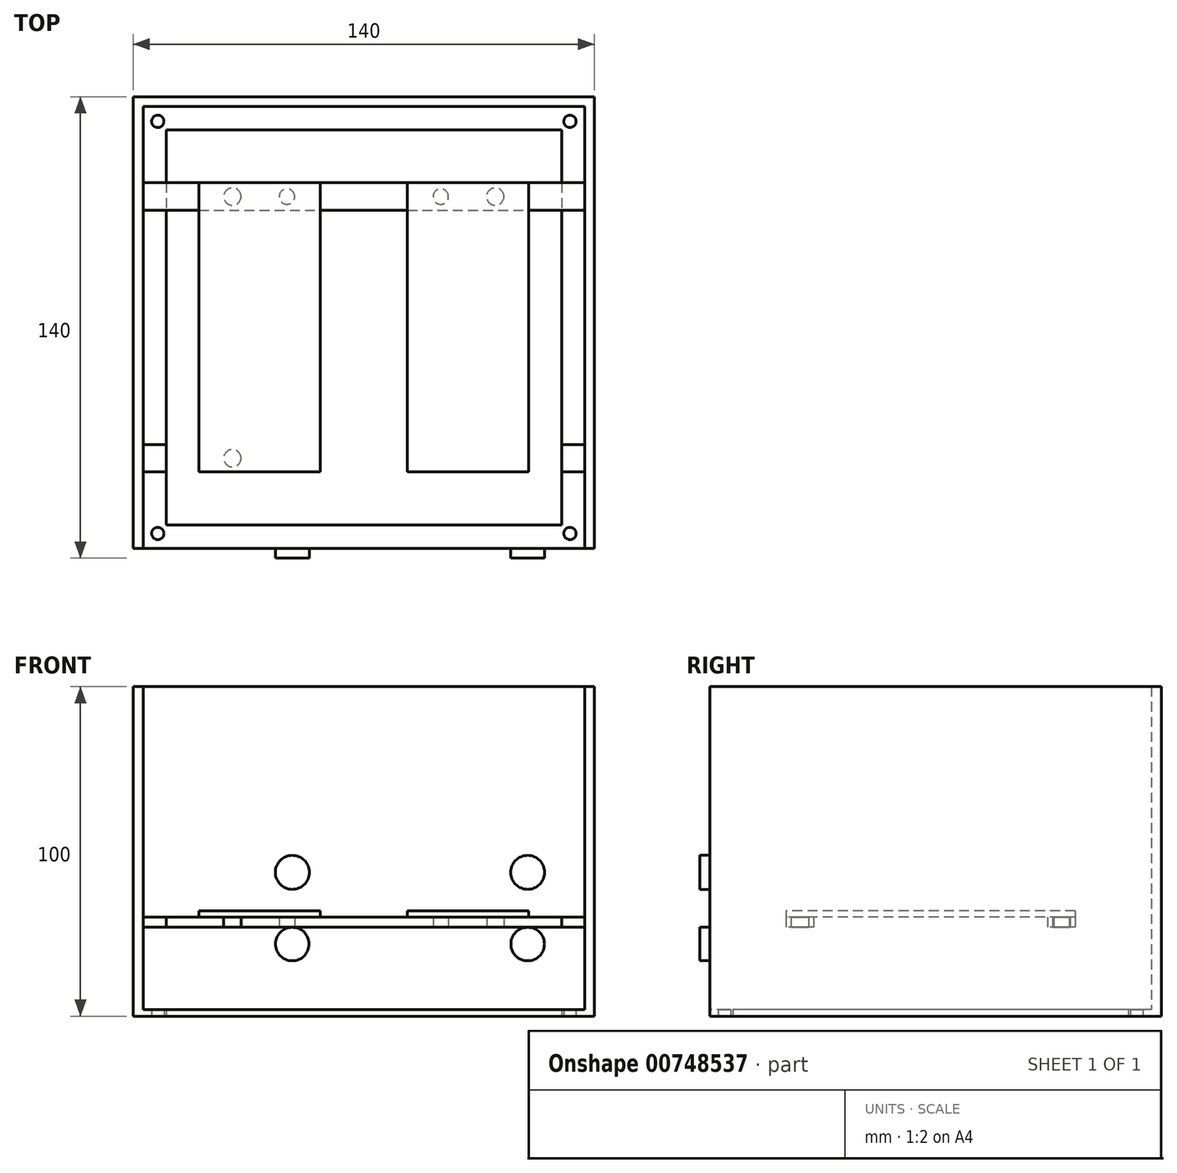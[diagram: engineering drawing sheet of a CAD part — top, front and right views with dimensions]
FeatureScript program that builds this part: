
annotation { "Feature Type Name" : "Feature", "Feature Type Description" : "" }
export const myFeature = defineFeature(function(context is Context, id is Id, definition is map)
    precondition{}
    {
        {
            var Q0;
            Q0=qCreatedBy(makeId("Top.planeOp"),FACE);
            var sketch = newSketch(context, id + "F0", { "sketchPlane" : qUnion([Q0])});
            skLineSegment(sketch, "E0.bottom", {"start": v(70, 70) * mm, "end": v(-70, 70) * mm});
            skLineSegment(sketch, "E0.top", {"start": v(70, -70) * mm, "end": v(-70, -70) * mm});
            skLineSegment(sketch, "E0.left", {"start": v(70, 70) * mm, "end": v(70, -70) * mm});
            skLineSegment(sketch, "E0.right", {"start": v(-70, 70) * mm, "end": v(-70, -70) * mm});
            skPoint(sketch, "E0.middle", {"position": v(0, 0) * mm});
            skLineSegment(sketch, "E1.bottom", {"start": v(60, 60) * mm, "end": v(-60, 60) * mm});
            skLineSegment(sketch, "E1.top", {"start": v(60, -60) * mm, "end": v(-60, -60) * mm});
            skLineSegment(sketch, "E1.left", {"start": v(60, 60) * mm, "end": v(60, -60) * mm});
            skLineSegment(sketch, "E1.right", {"start": v(-60, 60) * mm, "end": v(-60, -60) * mm});
            skLineSegment(sketch, "E2", {"start": v(60, 60) * mm, "end": v(70, 60) * mm, "construction": true});
            skLineSegment(sketch, "E3", {"start": v(60, 60) * mm, "end": v(70, 70) * mm, "construction": true});
            skCircle(sketch, "E4", {"center": v(62.53, 62.53) * mm, "radius": 1.87 * mm});
            skLineSegment(sketch, "E5.bottom", {"start": v(67, 67) * mm, "end": v(-67, 67) * mm});
            skLineSegment(sketch, "E5.top", {"start": v(67, -67) * mm, "end": v(-67, -67) * mm});
            skLineSegment(sketch, "E5.left", {"start": v(67, 67) * mm, "end": v(67, -67) * mm});
            skLineSegment(sketch, "E5.right", {"start": v(-67, 67) * mm, "end": v(-67, -67) * mm});
            skCircle(sketch, "E6.1.0", {"center": v(-62.53, 62.53) * mm, "radius": 1.87 * mm});
            skCircle(sketch, "E6.2.0", {"center": v(-62.53, -62.53) * mm, "radius": 1.87 * mm});
            skCircle(sketch, "E6.3.0", {"center": v(62.53, -62.53) * mm, "radius": 1.87 * mm});
            skLineSegment(sketch, "E7.bottom", {"start": v(-67, -35.52) * mm, "end": v(67, -35.52) * mm});
            skLineSegment(sketch, "E7.top", {"start": v(-67, -43.87) * mm, "end": v(67, -43.87) * mm});
            skLineSegment(sketch, "E7.left", {"start": v(-67, -35.52) * mm, "end": v(-67, -43.87) * mm});
            skLineSegment(sketch, "E7.right", {"start": v(67, -35.52) * mm, "end": v(67, -43.87) * mm});
            skLineSegment(sketch, "E8", {"start": v(-60, 0) * mm, "end": v(60, 0) * mm, "construction": true});
            skLineSegment(sketch, "E9.MirrorCS", {"start": v(-67, 35.52) * mm, "end": v(67, 35.52) * mm});
            skLineSegment(sketch, "E10.MirrorCS", {"start": v(-67, 43.87) * mm, "end": v(67, 43.87) * mm});
            skLineSegment(sketch, "E11", {"start": v(-39.88, 43.87) * mm, "end": v(-39.88, 35.52) * mm, "construction": true});
            skCircle(sketch, "E12", {"center": v(-39.88, 39.7) * mm, "radius": 2.63 * mm});
            skLineSegment(sketch, "E13", {"start": v(-23.34, 43.87) * mm, "end": v(-23.34, 35.52) * mm, "construction": true});
            skCircle(sketch, "E14", {"center": v(-23.34, 39.7) * mm, "radius": 2.35 * mm});
            skLineSegment(sketch, "E15", {"start": v(0, 35.52) * mm, "end": v(0, -35.52) * mm, "construction": true});
            skCircle(sketch, "E16.MirrorC", {"center": v(23.34, 39.7) * mm, "radius": 2.35 * mm});
            skCircle(sketch, "E17.MirrorC", {"center": v(39.88, 39.7) * mm, "radius": 2.63 * mm});
            skCircle(sketch, "E18.MirrorC", {"center": v(-39.88, -39.7) * mm, "radius": 2.63 * mm});
            skCircle(sketch, "E19.MirrorC", {"center": v(-23.34, -39.7) * mm, "radius": 2.35 * mm});
            skCircle(sketch, "E20.MirrorC", {"center": v(23.34, -39.7) * mm, "radius": 2.35 * mm});
            skCircle(sketch, "E21.MirrorC", {"center": v(39.88, -39.7) * mm, "radius": 2.63 * mm});
            skLineSegment(sketch, "E22", {"start": v(-39.88, 39.7) * mm, "end": v(-23.34, 39.7) * mm, "construction": true});
            skSolve(sketch);
        }
        {
            var Q0;
            {var subQ1=sQuery(id+"F0.wireOp",EDGE,"E1.bottom");Q0=makeQuery(id+"F0.imprint","IMPRINT",FACE,{"disambiguationData":[TD([[makeQuery(id+"F0.imprint","IMPRINT",EDGE,{"derivedFrom":subQ1}),-1.0]])]});}
            var Q1;
            Q1=makeQuery(id+"F0.imprint","IMPRINT",FACE,{"disambiguationData":[TD([[makeQuery(id+"F0.imprint","IMPRINT",EDGE,{"derivedFrom":sQuery(id+"F0.wireOp",EDGE,"E0.bottom")}),1.0]])]});
            var Q2;
            {var subQ0=sQuery(id+"F0.wireOp",EDGE,"E9.MirrorCS");var subQ1=sQuery(id+"F0.wireOp",EDGE,"E1.right");var subQ2=makeQuery(id+"F0.imprint","INTERSECT",VERTEX,{"derivedFrom":[subQ1,subQ0]});Q2=makeQuery(id+"F0.imprint","IMPRINT",FACE,{"disambiguationData":[TD([[makeQuery(id+"F0.imprint","IMPRINT",EDGE,{"disambiguationData":[TD([[subQ2,1.0]])],"derivedFrom":subQ1}),-1.0]])]});}
            var Q3;
            {var subQ0=sQuery(id+"F0.wireOp",EDGE,"E9.MirrorCS");var subQ1=sQuery(id+"F0.wireOp",EDGE,"E1.right");var subQ2=makeQuery(id+"F0.imprint","INTERSECT",VERTEX,{"derivedFrom":[subQ1,subQ0]});Q3=makeQuery(id+"F0.imprint","IMPRINT",FACE,{"disambiguationData":[TD([[makeQuery(id+"F0.imprint","IMPRINT",EDGE,{"disambiguationData":[TD([[subQ2,-1.0]])],"derivedFrom":subQ1}),-1.0]])]});}
            var Q4;
            {var subQ0=sQuery(id+"F0.wireOp",EDGE,"E7.bottom");var subQ1=sQuery(id+"F0.wireOp",EDGE,"E1.right");var subQ2=makeQuery(id+"F0.imprint","INTERSECT",VERTEX,{"derivedFrom":[subQ1,subQ0]});Q4=makeQuery(id+"F0.imprint","IMPRINT",FACE,{"disambiguationData":[TD([[makeQuery(id+"F0.imprint","IMPRINT",EDGE,{"disambiguationData":[TD([[subQ2,-1.0]])],"derivedFrom":subQ1}),-1.0]])]});}
            var Q5;
            {var subQ1=sQuery(id+"F0.wireOp",EDGE,"E1.top");Q5=makeQuery(id+"F0.imprint","IMPRINT",FACE,{"disambiguationData":[TD([[makeQuery(id+"F0.imprint","IMPRINT",EDGE,{"derivedFrom":subQ1}),1.0]])]});}
            var Q6;
            {var subQ0=sQuery(id+"F0.wireOp",EDGE,"E7.bottom");var subQ1=sQuery(id+"F0.wireOp",EDGE,"E1.left");var subQ2=makeQuery(id+"F0.imprint","INTERSECT",VERTEX,{"derivedFrom":[subQ1,subQ0]});Q6=makeQuery(id+"F0.imprint","IMPRINT",FACE,{"disambiguationData":[TD([[makeQuery(id+"F0.imprint","IMPRINT",EDGE,{"disambiguationData":[TD([[subQ2,-1.0]])],"derivedFrom":subQ1}),1.0]])]});}
            var Q7;
            {var subQ0=sQuery(id+"F0.wireOp",EDGE,"E9.MirrorCS");var subQ1=sQuery(id+"F0.wireOp",EDGE,"E1.left");var subQ2=makeQuery(id+"F0.imprint","INTERSECT",VERTEX,{"derivedFrom":[subQ1,subQ0]});Q7=makeQuery(id+"F0.imprint","IMPRINT",FACE,{"disambiguationData":[TD([[makeQuery(id+"F0.imprint","IMPRINT",EDGE,{"disambiguationData":[TD([[subQ2,-1.0]])],"derivedFrom":subQ1}),1.0]])]});}
            var Q8;
            {var subQ0=sQuery(id+"F0.wireOp",EDGE,"E9.MirrorCS");var subQ1=sQuery(id+"F0.wireOp",EDGE,"E1.left");var subQ2=makeQuery(id+"F0.imprint","INTERSECT",VERTEX,{"derivedFrom":[subQ1,subQ0]});Q8=makeQuery(id+"F0.imprint","IMPRINT",FACE,{"disambiguationData":[TD([[makeQuery(id+"F0.imprint","IMPRINT",EDGE,{"disambiguationData":[TD([[subQ2,1.0]])],"derivedFrom":subQ1}),1.0]])]});}
            extrude(context, id + "F1", {"entities" : qUnion([Q0, Q1, Q2, Q3, Q4, Q5, Q6, Q7, Q8]), "depth" : 2 * mm, "offsetDistance" : 25 * mm});
        }
        {
            var Q0;
            Q0=makeQuery(id+"F0.imprint","IMPRINT",FACE,{"disambiguationData":[TD([[makeQuery(id+"F0.imprint","IMPRINT",EDGE,{"derivedFrom":sQuery(id+"F0.wireOp",EDGE,"E0.bottom")}),1.0]])]});
            var Q1;
            Q1=makeQuery(id+"F1.opExtrude","CAP_FACE",FACE,{"disambiguationData":[OSD([sQuery(id+"F0.wireOp",EDGE,"E0.bottom"),sQuery(id+"F0.wireOp",EDGE,"E0.top"),sQuery(id+"F0.wireOp",EDGE,"E0.left"),sQuery(id+"F0.wireOp",EDGE,"E0.right"),sQuery(id+"F0.wireOp",EDGE,"E1.bottom"),sQuery(id+"F0.wireOp",EDGE,"E1.top"),sQuery(id+"F0.wireOp",EDGE,"E1.left"),sQuery(id+"F0.wireOp",EDGE,"E1.right"),sQuery(id+"F0.wireOp",EDGE,"E4"),sQuery(id+"F0.wireOp",EDGE,"E6.1.0"),sQuery(id+"F0.wireOp",EDGE,"E6.2.0"),sQuery(id+"F0.wireOp",EDGE,"E6.3.0")])],"isStart":false});
            extrude(context, id + "F2", {"entities" : qUnion([Q0]), "operationType" : NewBodyOperationType.ADD, "depth" : 100 * mm, "offsetDistance" : 25 * mm, "hasSecondDirection" : true, "secondDirectionBound" : SecondDirectionBoundingType.UP_TO_SURFACE, "secondDirectionOppositeDirection" : false, "secondDirectionDepth" : 19.3 * mm, "secondDirectionBoundEntityFace" : qUnion([Q1])});
        }
        {
            var Q0;
            Q0=makeQuery(id+"F0.imprint","IMPRINT",FACE,{"disambiguationData":[TD([[makeQuery(id+"F0.imprint","IMPRINT",EDGE,{"derivedFrom":sQuery(id+"F0.wireOp",EDGE,"E12")}),-1.0]])]});
            var Q1;
            {var subQ0=sQuery(id+"F0.wireOp",EDGE,"E9.MirrorCS");var subQ1=sQuery(id+"F0.wireOp",EDGE,"E1.right");var subQ2=makeQuery(id+"F0.imprint","INTERSECT",VERTEX,{"derivedFrom":[subQ1,subQ0]});Q1=makeQuery(id+"F0.imprint","IMPRINT",FACE,{"disambiguationData":[TD([[makeQuery(id+"F0.imprint","IMPRINT",EDGE,{"disambiguationData":[TD([[subQ2,1.0]])],"derivedFrom":subQ1}),-1.0]])]});}
            var Q2;
            {var subQ0=sQuery(id+"F0.wireOp",EDGE,"E9.MirrorCS");var subQ1=sQuery(id+"F0.wireOp",EDGE,"E1.left");var subQ2=makeQuery(id+"F0.imprint","INTERSECT",VERTEX,{"derivedFrom":[subQ1,subQ0]});Q2=makeQuery(id+"F0.imprint","IMPRINT",FACE,{"disambiguationData":[TD([[makeQuery(id+"F0.imprint","IMPRINT",EDGE,{"disambiguationData":[TD([[subQ2,1.0]])],"derivedFrom":subQ1}),1.0]])]});}
            var Q3;
            {var subQ0=sQuery(id+"F0.wireOp",EDGE,"E7.bottom");var subQ1=sQuery(id+"F0.wireOp",EDGE,"E1.left");var subQ2=makeQuery(id+"F0.imprint","INTERSECT",VERTEX,{"derivedFrom":[subQ1,subQ0]});Q3=makeQuery(id+"F0.imprint","IMPRINT",FACE,{"disambiguationData":[TD([[makeQuery(id+"F0.imprint","IMPRINT",EDGE,{"disambiguationData":[TD([[subQ2,-1.0]])],"derivedFrom":subQ1}),1.0]])]});}
            var Q4;
            Q4=makeQuery(id+"F0.imprint","IMPRINT",FACE,{"disambiguationData":[TD([[makeQuery(id+"F0.imprint","IMPRINT",EDGE,{"derivedFrom":sQuery(id+"F0.wireOp",EDGE,"E18.MirrorC")}),1.0]])]});
            var Q5;
            {var subQ0=sQuery(id+"F0.wireOp",EDGE,"E7.bottom");var subQ1=sQuery(id+"F0.wireOp",EDGE,"E1.right");var subQ2=makeQuery(id+"F0.imprint","INTERSECT",VERTEX,{"derivedFrom":[subQ1,subQ0]});Q5=makeQuery(id+"F0.imprint","IMPRINT",FACE,{"disambiguationData":[TD([[makeQuery(id+"F0.imprint","IMPRINT",EDGE,{"disambiguationData":[TD([[subQ2,-1.0]])],"derivedFrom":subQ1}),-1.0]])]});}
            extrude(context, id + "F3", {"entities" : qUnion([Q0, Q1, Q2, Q3, Q4, Q5]), "operationType" : NewBodyOperationType.ADD, "depth" : 30 * mm, "offsetDistance" : 25 * mm, "hasSecondDirection" : true, "secondDirectionOppositeDirection" : false, "secondDirectionDepth" : 27 * mm});
        }
        {
            var Q0;
            {var subQ0=sQuery(id+"F0.wireOp",EDGE,"E0.top");Q0=makeQuery(id+"F2.boolean.opBoolean","MERGE",FACE,{"derivedFrom":[makeQuery(id+"F1.opExtrude","SWEPT_FACE",FACE,{"disambiguationData":[OSD([subQ0])]}),makeQuery(id+"F2.opExtrude","SWEPT_FACE",FACE,{"disambiguationData":[OSD([subQ0])]})]});}
            var sketch = newSketch(context, id + "F4", { "sketchPlane" : qUnion([Q0])});
            skLineSegment(sketch, "E23", {"start": v(-70, 21.87) * mm, "end": v(70, 21.87) * mm, "construction": true});
            skLineSegment(sketch, "E24", {"start": v(-70, 43.64) * mm, "end": v(70, 43.64) * mm, "construction": true});
            skCircle(sketch, "E25", {"center": v(-49.71, 43.64) * mm, "radius": 5.15 * mm});
            skPoint(sketch, "E26", {"position": v(0, 43.64) * mm});
            skCircle(sketch, "E27", {"center": v(-49.71, 21.87) * mm, "radius": 5.08 * mm});
            skLineSegment(sketch, "E28", {"start": v(0, 0) * mm, "end": v(0, 100) * mm, "construction": true});
            skLineSegment(sketch, "E29", {"start": v(-35.71, 100) * mm, "end": v(-35.71, 0) * mm, "construction": true});
            skCircle(sketch, "E30.MirrorC", {"center": v(-21.71, 43.64) * mm, "radius": 5.15 * mm});
            skCircle(sketch, "E31.MirrorC", {"center": v(-21.71, 21.87) * mm, "radius": 5.08 * mm});
            skLineSegment(sketch, "E32", {"start": v(-50.71, 82.39) * mm, "end": v(-50.71, 67.39) * mm});
            skLineSegment(sketch, "E33.MirrorCS", {"start": v(-20.71, 82.39) * mm, "end": v(-20.71, 67.39) * mm});
            skLineSegment(sketch, "E34", {"start": v(-50.71, 82.39) * mm, "end": v(-20.71, 82.39) * mm});
            skLineSegment(sketch, "E35", {"start": v(-20.71, 67.39) * mm, "end": v(-50.71, 67.39) * mm});
            skLineSegment(sketch, "E36.MirrorCS", {"start": v(20.71, 67.39) * mm, "end": v(50.71, 67.39) * mm});
            skLineSegment(sketch, "E37.MirrorCS", {"start": v(20.71, 82.39) * mm, "end": v(20.71, 67.39) * mm});
            skLineSegment(sketch, "E38.MirrorCS", {"start": v(50.71, 82.39) * mm, "end": v(20.71, 82.39) * mm});
            skLineSegment(sketch, "E39.MirrorCS", {"start": v(50.71, 82.39) * mm, "end": v(50.71, 67.39) * mm});
            skCircle(sketch, "E40.MirrorC", {"center": v(49.71, 43.64) * mm, "radius": 5.15 * mm});
            skCircle(sketch, "E41.MirrorC", {"center": v(21.71, 43.64) * mm, "radius": 5.15 * mm});
            skCircle(sketch, "E42.MirrorC", {"center": v(21.71, 21.87) * mm, "radius": 5.08 * mm});
            skCircle(sketch, "E43.MirrorC", {"center": v(49.71, 21.87) * mm, "radius": 5.08 * mm});
            skSolve(sketch);
        }
        {
            var Q0;
            Q0=makeQuery(id+"F4.imprint","IMPRINT",FACE,{"disambiguationData":[TD([[makeQuery(id+"F4.imprint","IMPRINT",EDGE,{"derivedFrom":sQuery(id+"F4.wireOp",EDGE,"E32")}),1.0]])]});
            var Q1;
            Q1=makeQuery(id+"F4.imprint","IMPRINT",FACE,{"disambiguationData":[TD([[makeQuery(id+"F4.imprint","IMPRINT",EDGE,{"derivedFrom":sQuery(id+"F4.wireOp",EDGE,"E36.MirrorCS")}),1.0]])]});
            var Q2;
            Q2=makeQuery(id+"F4.imprint","IMPRINT",FACE,{"disambiguationData":[TD([[makeQuery(id+"F4.imprint","IMPRINT",EDGE,{"derivedFrom":sQuery(id+"F4.wireOp",EDGE,"E40.MirrorC")}),-1.0]])]});
            var Q3;
            Q3=makeQuery(id+"F4.imprint","IMPRINT",FACE,{"disambiguationData":[TD([[makeQuery(id+"F4.imprint","IMPRINT",EDGE,{"derivedFrom":sQuery(id+"F4.wireOp",EDGE,"E41.MirrorC")}),1.0]])]});
            var Q4;
            Q4=makeQuery(id+"F4.imprint","IMPRINT",FACE,{"disambiguationData":[TD([[makeQuery(id+"F4.imprint","IMPRINT",EDGE,{"derivedFrom":sQuery(id+"F4.wireOp",EDGE,"E42.MirrorC")}),1.0]])]});
            var Q5;
            Q5=makeQuery(id+"F4.imprint","IMPRINT",FACE,{"disambiguationData":[TD([[makeQuery(id+"F4.imprint","IMPRINT",EDGE,{"derivedFrom":sQuery(id+"F4.wireOp",EDGE,"E43.MirrorC")}),-1.0]])]});
            var Q6;
            Q6=makeQuery(id+"F4.imprint","IMPRINT",FACE,{"disambiguationData":[TD([[makeQuery(id+"F4.imprint","IMPRINT",EDGE,{"derivedFrom":sQuery(id+"F4.wireOp",EDGE,"E30.MirrorC")}),-1.0]])]});
            var Q7;
            Q7=makeQuery(id+"F4.imprint","IMPRINT",FACE,{"disambiguationData":[TD([[makeQuery(id+"F4.imprint","IMPRINT",EDGE,{"derivedFrom":sQuery(id+"F4.wireOp",EDGE,"E25")}),1.0]])]});
            var Q8;
            Q8=makeQuery(id+"F4.imprint","IMPRINT",FACE,{"disambiguationData":[TD([[makeQuery(id+"F4.imprint","IMPRINT",EDGE,{"derivedFrom":sQuery(id+"F4.wireOp",EDGE,"E27")}),1.0]])]});
            var Q9;
            Q9=makeQuery(id+"F4.imprint","IMPRINT",FACE,{"disambiguationData":[TD([[makeQuery(id+"F4.imprint","IMPRINT",EDGE,{"derivedFrom":sQuery(id+"F4.wireOp",EDGE,"E31.MirrorC")}),-1.0]])]});
            var Q10;
            Q10=makeQuery(id+"F2.opExtrude","SWEPT_FACE",FACE,{"disambiguationData":[OSD([sQuery(id+"F0.wireOp",EDGE,"E5.top")])]});
            extrude(context, id + "F5", {"entities" : qUnion([Q0, Q1, Q2, Q3, Q4, Q5, Q6, Q7, Q8, Q9]), "operationType" : NewBodyOperationType.REMOVE, "endBound" : BoundingType.UP_TO_SURFACE, "oppositeDirection" : true, "depth" : 25 * mm, "endBoundEntityFace" : qUnion([Q10]), "offsetDistance" : 25 * mm});
        }
        {
            var Q0;
            Q0=makeQuery(id+"F3.opExtrude","CAP_FACE",FACE,{"disambiguationData":[OSD([sQuery(id+"F0.wireOp",EDGE,"E5.left"),sQuery(id+"F0.wireOp",EDGE,"E5.right"),sQuery(id+"F0.wireOp",EDGE,"E9.MirrorCS"),sQuery(id+"F0.wireOp",EDGE,"E10.MirrorCS"),sQuery(id+"F0.wireOp",EDGE,"E12"),sQuery(id+"F0.wireOp",EDGE,"E14"),sQuery(id+"F0.wireOp",EDGE,"E16.MirrorC"),sQuery(id+"F0.wireOp",EDGE,"E17.MirrorC")])],"isStart":false});
            var sketch = newSketch(context, id + "F6", { "sketchPlane" : qUnion([Q0])});
            skLineSegment(sketch, "E44.bottom", {"start": v(-50.04, 43.87) * mm, "end": v(-13.18, 43.87) * mm});
            skLineSegment(sketch, "E44.top", {"start": v(-50.04, -43.87) * mm, "end": v(-13.18, -43.87) * mm});
            skLineSegment(sketch, "E44.left", {"start": v(-50.04, 43.87) * mm, "end": v(-50.04, -43.87) * mm});
            skLineSegment(sketch, "E44.right", {"start": v(-13.18, 43.87) * mm, "end": v(-13.18, -43.87) * mm});
            skLineSegment(sketch, "E45", {"start": v(-39.88, 39.7) * mm, "end": v(-50.04, 39.7) * mm, "construction": true});
            skLineSegment(sketch, "E46", {"start": v(-23.34, 39.7) * mm, "end": v(-13.18, 39.7) * mm, "construction": true});
            skSolve(sketch);
        }
        {
            var Q0;
            Q0 = qSketchRegion(id + "F6", true);
            extrude(context, id + "F7", {"entities" : qUnion([Q0]), "depth" : 2 * mm, "offsetDistance" : 25 * mm});
        }
        {
            var Q0;
            Q0=makeQuery(id+"F7.opExtrude","SWEPT_BODY",BODY,{"disambiguationData":[OSD([sQuery(id+"F6.wireOp",EDGE,"E44.bottom"),sQuery(id+"F6.wireOp",EDGE,"E44.top"),sQuery(id+"F6.wireOp",EDGE,"E44.left"),sQuery(id+"F6.wireOp",EDGE,"E44.right")])]});
            var Q1;
            Q1=qCreatedBy(makeId("Right.planeOp"),FACE);
            mirror(context, id + "F8", {"entities" : qUnion([Q0]), "mirrorPlane" : qUnion([Q1])});
        }
    });
